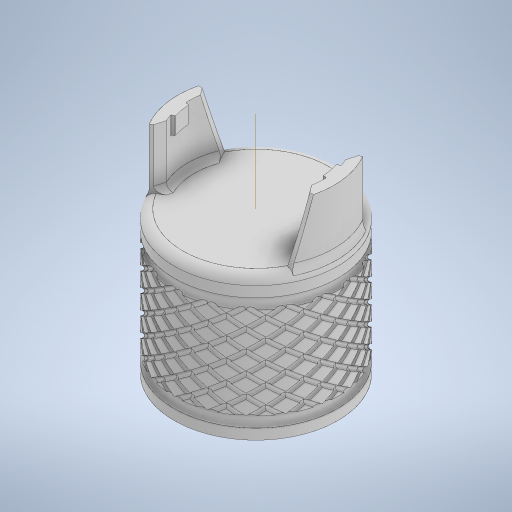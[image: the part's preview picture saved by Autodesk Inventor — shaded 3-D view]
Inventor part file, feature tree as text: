
AUTODESK INVENTOR PART (.ipt)
format: ipt  version: 2023 (Build 270158030, 158C)  size: 2,339,328 bytes
history: native  units: mm
features: sketch x7, projected_geometry x6, extrude x5, fillet x3, chamfer x2, pattern_circular x2, plane x1, revolve x1, helix x1, mirror x1
ambient origin geometry x8: Origin, YZ Plane, XZ Plane, XY Plane, X Axis, Y Axis, Z Axis, Center Point
bodies: Solid1 (feature_tree)
feature tree (29):
  extrude  "Extrusion1"  Depth=16.3mm TaperAngle=0.0deg
  extrude  "tooth"  Depth=7.8mm
  extrude  "Extrusion3"  Depth=6.8mm TaperAngle=0.0deg
  chamfer  "Chamfer1"  Distance=2.0mm
  plane  "Work Plane2"
  extrude  "Extrusion4"  Depth=2.0mm
  chamfer  "Chamfer2"  Distance=20.0mm
  fillet  "Fillet1"  Radius=0.7mm
  pattern_circular  "Circular Pattern1"  Count=2 Angle=360.0deg
  extrude  "rod-insertion"  Depth=2.0mm
  fillet  "Fillet2"  Radius=3.535mm
  revolve  "Revolution1"  [1 undecoded]
  helix  "Coil1"  [1 undecoded]
  mirror  "Mirror1"
  pattern_circular  "Circular Pattern2"  [2 undecoded]
  fillet  "Fillet3"  Radius=1.0mm
  sketch  "Sketch1"  dims[d0=18.7mm d1=16.3mm d2=0.0mm]
  sketch  "Sketch2"  dims[d3=1.6mm d4=7.8mm]
  projected_geometry  "Projected Loop1"
  sketch  "Sketch4"  dims[d5=3.9mm d6=6.8mm d7=0.0mm]
  projected_geometry  "Projected Loop2"
  sketch  "Sketch6"  dims[d8=1.7mm]
  projected_geometry  "Projected Loop3"
  projected_geometry  "Projected Loop4"
  sketch  "Sketch7"  dims[d9=2.0mm d12=2.0mm d13=0.0mm]
  sketch  "Sketch8"  dims[d14=0.08mm d15=2.0mm d16=45.0deg d17=6.0mm d18=20.0mm d19=0.0mm]
  projected_geometry  "Projected Loop5"
  sketch  "Sketch9"  dims[d20=0.8mm d21=2.0mm d22=45.0deg d23=0.7mm d24=20.0mm d25=360.0deg d27=7.07mm d28=3.535mm d29=10.0mm d30=3.5mm d31=7.0mm d32=12.5mm d33=0.0mm d34=1.0mm d35=1.8mm d36=1.8mm d37=1.2mm d38=9.35mm d39=9.35mm d40=90.0deg d41=0.6mm d42=9.35mm d45=40.0mm d46=11.5mm d47=20.0mm d48=0.0mm d49=90.0deg d50=90.0deg d51=0.0mm d52=0.0mm d53=10.5mm d54=0.3mm d55=180.0mm d56=360.0deg d58=1.172702mm d59=0.4mm d60=2.0mm]
  projected_geometry  "Projected Loop6"
note: 4 required parameter values undecoded (feature->parameter linkage not recoverable at this tier; creation-order binding heuristic only, values carry confidence <= 0.55)